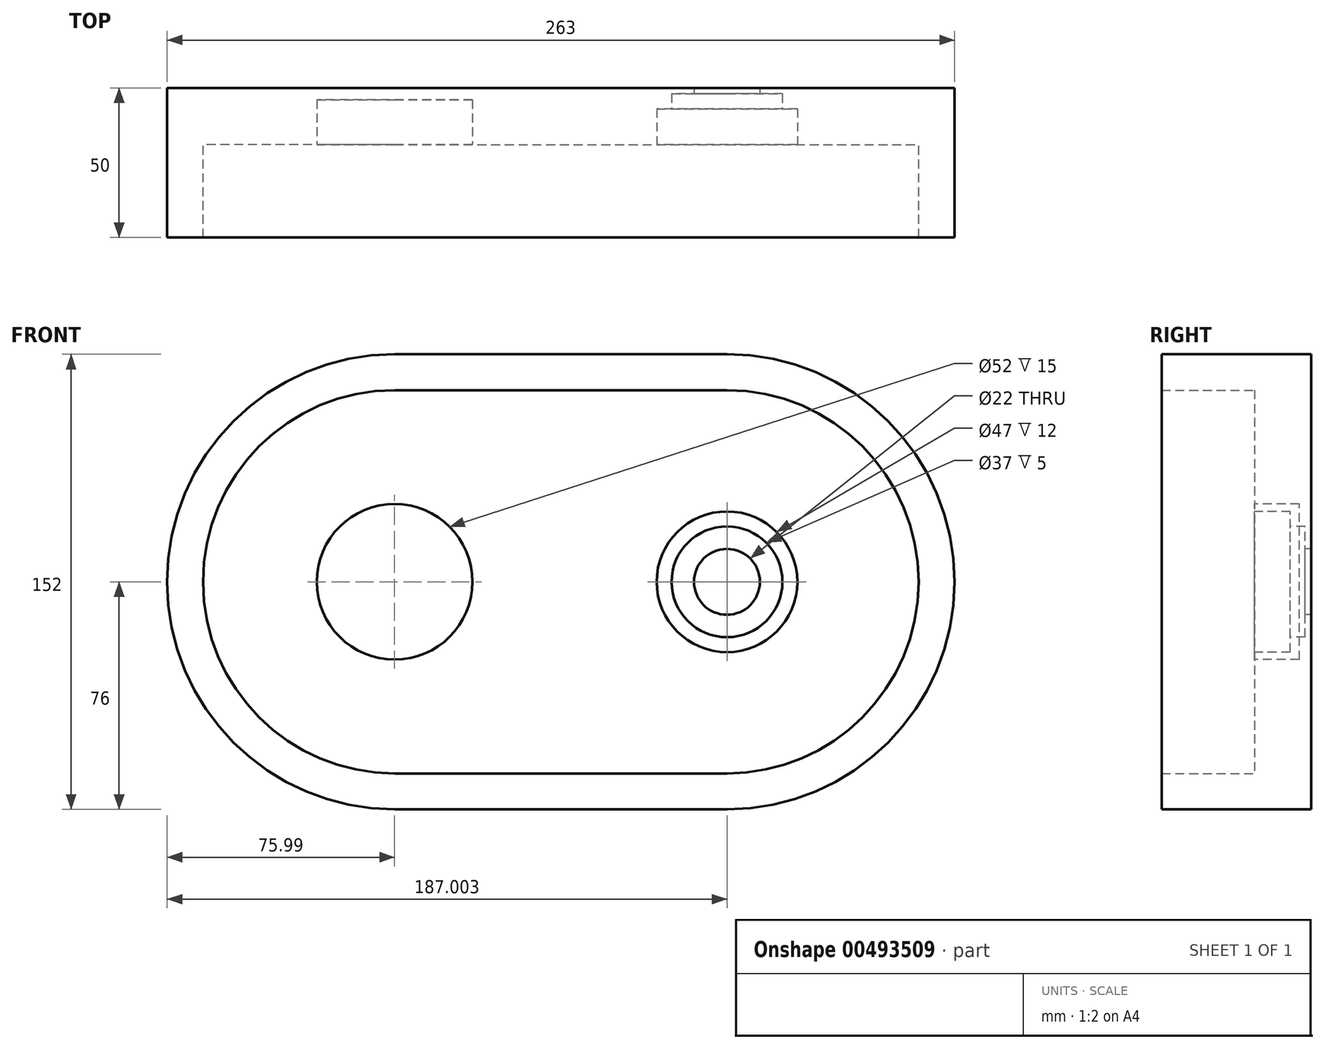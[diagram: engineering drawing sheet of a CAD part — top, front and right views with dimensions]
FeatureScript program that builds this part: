
annotation { "Feature Type Name" : "Feature", "Feature Type Description" : "" }
export const myFeature = defineFeature(function(context is Context, id is Id, definition is map)
    precondition{}
    {
        {
            var Q0;
            Q0=qCreatedBy(makeId("Front.planeOp"),FACE);
            var sketch = newSketch(context, id + "F0", { "sketchPlane" : qUnion([Q0])});
            skArc(sketch, "E0", {"start": v(76.01, 76) * mm, "mid": v(0.01, 0) * mm, "end": v(76.01, -76) * mm});
            skArc(sketch, "E1", {"start": v(187.01, -76) * mm, "mid": v(263.01, 0) * mm, "end": v(187.01, 76) * mm});
            skLineSegment(sketch, "E2", {"start": v(76.01, -76) * mm, "end": v(187.01, -76) * mm});
            skLineSegment(sketch, "E3", {"start": v(76.01, 76) * mm, "end": v(187.01, 76) * mm});
            skArc(sketch, "E4", {"start": v(76.01, 64) * mm, "mid": v(12.01, 0) * mm, "end": v(76.01, -64) * mm});
            skArc(sketch, "E5", {"start": v(187.01, -64) * mm, "mid": v(251.01, 0) * mm, "end": v(187.01, 64) * mm});
            skLineSegment(sketch, "E6", {"start": v(76.01, 64) * mm, "end": v(187.01, 64) * mm});
            skLineSegment(sketch, "E7", {"start": v(76.01, -64) * mm, "end": v(187.01, -64) * mm});
            skSolve(sketch);
        }
        {
            var Q0;
            Q0=makeQuery(id+"F0.imprint","IMPRINT",FACE,{"disambiguationData":[TD([[makeQuery(id+"F0.imprint","IMPRINT",EDGE,{"derivedFrom":sQuery(id+"F0.wireOp",EDGE,"E0")}),1.0]])]});
            var Q1;
            Q1=makeQuery(id+"F0.imprint","IMPRINT",FACE,{"disambiguationData":[TD([[makeQuery(id+"F0.imprint","IMPRINT",EDGE,{"derivedFrom":sQuery(id+"F0.wireOp",EDGE,"E4")}),1.0]])]});
            extrude(context, id + "F1", {"entities" : qUnion([Q0, Q1]), "depth" : 50 * mm, "offsetDistance" : 25 * mm});
        }
        {
            var Q0;
            Q0=qCreatedBy(makeId("Front.planeOp"),FACE);
            cPlane(context, id + "F2", {"entities" : qUnion([Q0]), "cplaneType" : CPlaneType.OFFSET, "offset" : 19 * mm, "width" : 150 * mm, "height" : 150 * mm});
        }
        {
            var Q0;
            Q0=qCreatedBy(id+"F2.planeOp",FACE);
            var sketch = newSketch(context, id + "F3", { "sketchPlane" : qUnion([Q0])});
            skArc(sketch, "E8", {"start": v(76.01, 64) * mm, "mid": v(12.01, 0) * mm, "end": v(76.01, -64) * mm});
            skArc(sketch, "E9", {"start": v(187.01, -64) * mm, "mid": v(251.01, 0) * mm, "end": v(187.01, 64) * mm});
            skLineSegment(sketch, "E10", {"start": v(76.01, 64) * mm, "end": v(187.01, 64) * mm});
            skLineSegment(sketch, "E11", {"start": v(76.01, -64) * mm, "end": v(187.01, -64) * mm});
            skSolve(sketch);
        }
        {
            var Q0;
            Q0 = qSketchRegion(id + "F3", true);
            extrude(context, id + "F4", {"entities" : qUnion([Q0]), "operationType" : NewBodyOperationType.REMOVE, "depth" : 200 * mm, "offsetDistance" : 25 * mm});
        }
        {
            var Q0;
            Q0=makeQuery(id+"F3.imprint","IMPRINT",FACE,{"disambiguationData":[TD([[makeQuery(id+"F3.imprint","IMPRINT",EDGE,{"derivedFrom":sQuery(id+"F3.wireOp",EDGE,"E8")}),1.0]])]});
            var sketch = newSketch(context, id + "F5", { "sketchPlane" : qUnion([Q0])});
            skCircle(sketch, "E12", {"center": v(76, 0) * mm, "radius": 26 * mm});
            skSolve(sketch);
        }
        {
            var Q0;
            Q0=makeQuery(id+"F5.imprint","IMPRINT",FACE,{"disambiguationData":[TD([[makeQuery(id+"F5.imprint","IMPRINT",EDGE,{"derivedFrom":sQuery(id+"F5.wireOp",EDGE,"E12")}),1.0]])]});
            var Q1;
            Q1=sQuery(id+"F5.wireOp",EDGE,"E12");
            extrude(context, id + "F6", {"entities" : qUnion([Q0]), "operationType" : NewBodyOperationType.REMOVE, "surfaceEntities" : qUnion([Q1]), "oppositeDirection" : true, "depth" : 15 * mm, "offsetDistance" : 25 * mm});
        }
        {
            var Q0;
            Q0=makeQuery(id+"F3.imprint","IMPRINT",FACE,{"disambiguationData":[TD([[makeQuery(id+"F3.imprint","IMPRINT",EDGE,{"derivedFrom":sQuery(id+"F3.wireOp",EDGE,"E8")}),1.0]])]});
            var sketch = newSketch(context, id + "F7", { "sketchPlane" : qUnion([Q0])});
            skLineSegment(sketch, "E13", {"start": v(187.01, 0) * mm, "end": v(187.01, -47.94) * mm, "construction": true});
            skSolve(sketch);
        }
        {
            var Q0;
            Q0=sQuery(id+"F7.wireOp",EDGE,"E13");
            cPlane(context, id + "F8", {"entities" : qUnion([Q0]), "cplaneType" : CPlaneType.LINE_ANGLE, "offset" : 25 * mm, "angle" : 0 * degree, "width" : 150 * mm, "height" : 150 * mm});
        }
        {
            var Q0;
            Q0=qCreatedBy(id+"F8.planeOp",FACE);
            var sketch = newSketch(context, id + "F9", { "sketchPlane" : qUnion([Q0])});
            skLineSegment(sketch, "E14", {"start": v(0, 0) * mm, "end": v(13.06, 0) * mm, "construction": true});
            skLineSegment(sketch, "E15", {"start": v(-8.94, 11) * mm, "end": v(2, 11) * mm});
            skLineSegment(sketch, "E16", {"start": v(2, 11) * mm, "end": v(2, 18.5) * mm});
            skLineSegment(sketch, "E17", {"start": v(2, 18.5) * mm, "end": v(7, 18.5) * mm});
            skLineSegment(sketch, "E18", {"start": v(7, 18.5) * mm, "end": v(7, 23.5) * mm});
            skLineSegment(sketch, "E19", {"start": v(7, 23.5) * mm, "end": v(19, 23.5) * mm});
            skLineSegment(sketch, "E20", {"start": v(19, 23.5) * mm, "end": v(19, 0) * mm});
            skLineSegment(sketch, "E21", {"start": v(-8.94, 11) * mm, "end": v(-8.94, 0) * mm});
            skLineSegment(sketch, "E22", {"start": v(-8.94, 0) * mm, "end": v(19, 0) * mm});
            skSolve(sketch);
        }
        {
            var Q0;
            Q0=makeQuery(id+"F9.imprint","IMPRINT",FACE,{"disambiguationData":[TD([[makeQuery(id+"F9.imprint","IMPRINT",EDGE,{"derivedFrom":sQuery(id+"F9.wireOp",EDGE,"E15")}),-1.0]])]});
            var Q1;
            Q1=sQuery(id+"F9.wireOp",EDGE,"E22");
            revolve(context, id + "F10", {"operationType" : NewBodyOperationType.REMOVE, "entities" : qUnion([Q0]), "axis" : qUnion([Q1]), "revolveType" : RevolveType.FULL, "oppositeDirection" : true});
        }
    });
